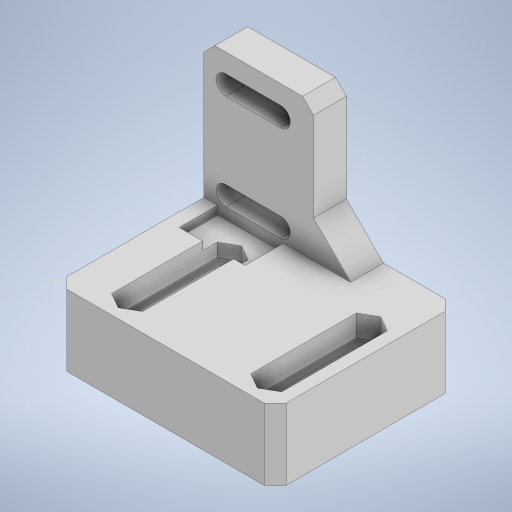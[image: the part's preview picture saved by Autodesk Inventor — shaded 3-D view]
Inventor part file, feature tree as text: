
AUTODESK INVENTOR PART (.ipt)
format: ipt  version: 2024 (Build 280153020, 153B)  size: 351,744 bytes
history: native  units: in
note: dims shown in document units (in); Inventor stores cm internally (conversion verified against a paired STEP export)
features: sketch x8, extrude x7, chamfer x4
ambient origin geometry x8: Origin, YZ Plane, XZ Plane, XY Plane, X Axis, Y Axis, Z Axis, Center Point
bodies: Solid1 (feature_tree)
feature tree (19):
  extrude  "Extrusion1"  Depth=1.063in
  extrude  "Extrusion2"  Depth=0.2362in
  extrude  "Extrusion3"  Depth=1.5748in TaperAngle=0.0deg
  sketch  "Sketch4"  dims[d8=0.1969in d9=0.1969in]
  extrude  "Extrusion4"  Depth=0.1969in
  extrude  "Extrusion5"  Depth=1.0in
  extrude  "Extrusion6"  Depth=1.0in
  chamfer  "Chamfer1"  Distance=1.5748in
  chamfer  "Chamfer2"  Distance=0.111in
  chamfer  "Chamfer3"  Distance=0.111in
  chamfer  "Chamfer4"  Distance=0.1575in
  extrude  "Extrusion7"  Depth=0.0591in
  sketch  "Sketch1"  dims[d0=0.5118in d1=1.063in]
  sketch  "Sketch2"  dims[d2=1.5748in d3=0.0in d4=0.2362in]
  sketch  "Sketch3"  dims[d5=1.4961in d6=1.5748in d7=0.0in]
  sketch  "Sketch5"  dims[d10=0.6299in d11=1.0in]
  sketch  "Sketch6"  dims[d12=0.1299in d13=0.1969in d14=0.6299in d15=1.0in d16=0.1299in d17=1.5748in d18=0.0in]
  sketch  "Sketch7"  dims[d19=0.111in]
  sketch  "Sketch8"  dims[d20=0.111in d21=0.111in d23=0.111in d24=0.111in d25=0.111in d26=0.1575in d27=0.0in d28=0.0906in d29=0.689in d30=0.1575in d31=0.3937in d32=0.3937in d33=0.1378in d34=0.1378in d35=1.405in d36=0.0in d37=1.7825in d38=0.0in d39=0.2662in d40=0.0787in d41=45.0deg d42=0.0787in d43=0.0787in d44=45.0deg d45=0.0787in d46=0.0787in d47=45.0deg d48=0.0787in d49=0.0787in d50=45.0deg d53=0.0984in d54=0.4724in d55=0.2756in d56=0.0591in d57=0.0in]
